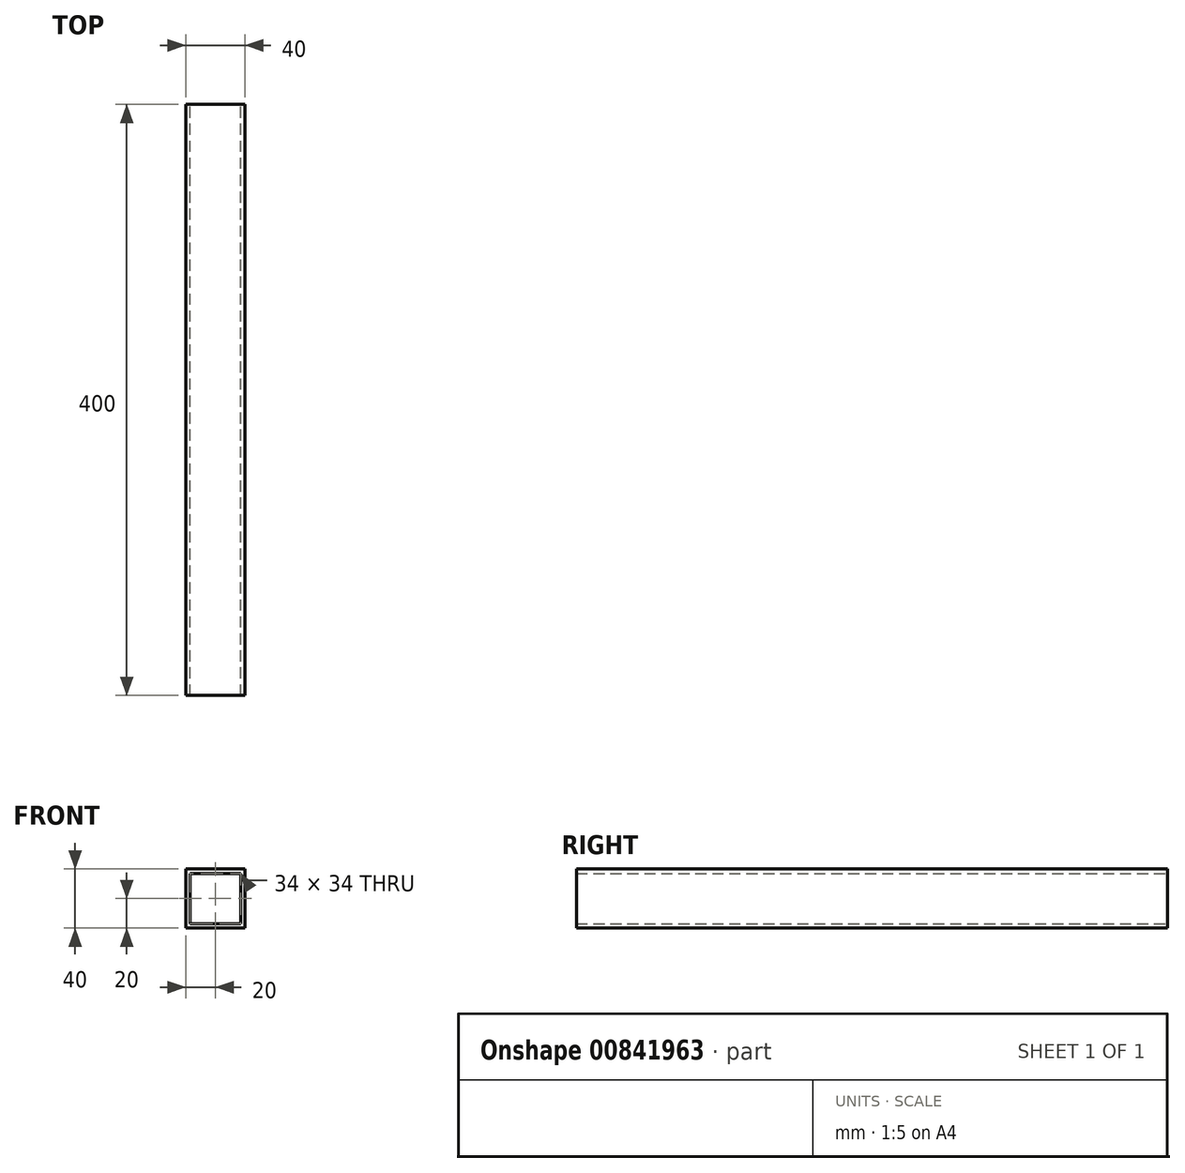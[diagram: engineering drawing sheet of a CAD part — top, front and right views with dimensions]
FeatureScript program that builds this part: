
annotation { "Feature Type Name" : "Feature", "Feature Type Description" : "" }
export const myFeature = defineFeature(function(context is Context, id is Id, definition is map)
    precondition{}
    {
        {
            var Q0;
            Q0=qCreatedBy(makeId("Front.planeOp"),FACE);
            var sketch = newSketch(context, id + "F0", { "sketchPlane" : qUnion([Q0])});
            skLineSegment(sketch, "E0.bottom", {"start": v(-20, 20) * mm, "end": v(20, 20) * mm});
            skLineSegment(sketch, "E0.top", {"start": v(-20, -20) * mm, "end": v(20, -20) * mm});
            skLineSegment(sketch, "E0.left", {"start": v(-20, 20) * mm, "end": v(-20, -20) * mm});
            skLineSegment(sketch, "E0.right", {"start": v(20, 20) * mm, "end": v(20, -20) * mm});
            skLineSegment(sketch, "E1.0", {"start": v(-17, 17) * mm, "end": v(-17, -17) * mm});
            skLineSegment(sketch, "E1.1", {"start": v(-17, 17) * mm, "end": v(17, 17) * mm});
            skLineSegment(sketch, "E1.2", {"start": v(17, 17) * mm, "end": v(17, -17) * mm});
            skLineSegment(sketch, "E1.3", {"start": v(-17, -17) * mm, "end": v(17, -17) * mm});
            skSolve(sketch);
        }
        {
            var Q0;
            Q0=makeQuery(id+"F0.imprint","IMPRINT",FACE,{"disambiguationData":[TD([[makeQuery(id+"F0.imprint","IMPRINT",EDGE,{"derivedFrom":sQuery(id+"F0.wireOp",EDGE,"E0.bottom")}),-1.0]])]});
            extrude(context, id + "F1", {"entities" : qUnion([Q0]), "endBound" : BoundingType.SYMMETRIC, "depth" : 400 * mm, "offsetDistance" : 25 * mm});
        }
    });
